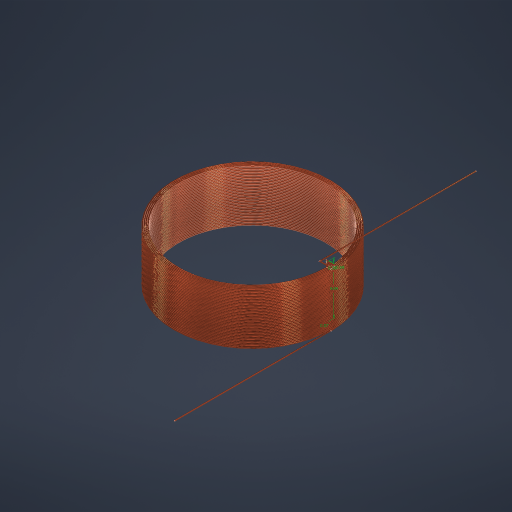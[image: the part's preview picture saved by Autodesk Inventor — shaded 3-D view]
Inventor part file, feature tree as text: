
AUTODESK INVENTOR PART (.ipt)
format: ipt  version: 2024.2 (Build 282272000, 272)  size: 3,379,712 bytes
history: native  units: mm
features: other x9, sketch x9, chamfer x8, sweep x4, extrude x1
ambient origin geometry x8: Origin, YZ Plane, XZ Plane, XY Plane, X Axis, Y Axis, Z Axis, Center Point
bodies: Volumenkörper1 (feature_tree), Volumenkörper2 (feature_tree), Volumenkörper3 (feature_tree), Volumenkörper4 (feature_tree), Volumenkörper5 (feature_tree), Volumenkörper6 (feature_tree), Volumenkörper7 (feature_tree), Volumenkörper8 (feature_tree), Volumenkörper9 (feature_tree)
feature tree (31):
  other  "Spirale1"
  other  "Spirale2"
  other  "Spirale3"
  other  "Spirale4"
  sweep  "Sweeping1"
  other  "3D-Skizze7"
  sketch  "Skizze15"  dims[d26=0.101mm d27=4.0mm d28=400.0mm d29=0.0mm d30=90.0deg d31=90.0deg d32=0.0mm d33=0.0mm]
  sweep  "Sweeping2"
  sweep  "Sweeping3"
  chamfer  "Fasen4"  Distance=0.7mm
  chamfer  "Fasen5"  [1 undecoded]
  chamfer  "Fasen6"  Distance=0.39mm
  chamfer  "Fasen7"  Distance=0.59mm
  chamfer  "Fasen8"  Distance=4.04mm
  chamfer  "Fasen9"  Distance=0.57mm
  extrude  "Extrusion1"  TaperAngle=0.0deg  [1 undecoded]
  chamfer  "Fasen10"  Distance=0.37mm
  sweep  "Sweeping4"
  chamfer  "Fasen11"  Distance=0.33mm
  other  "Kombinieren3"
  sketch  "Skizze1"  dims[d0=0.1mm d1=6.0mm]
  other  "3D-Skizze5"
  sketch  "Skizze14"  dims[d16=0.1mm d17=5.6995mm d18=0.101mm d19=4.0mm d20=400.0mm d21=0.0mm d22=90.0deg d23=90.0deg d24=0.0mm d25=0.0mm]
  sketch  "Skizze16"  dims[d34=0.101mm d35=4.0mm d36=400.0mm d37=0.0mm d38=90.0deg d39=90.0deg d40=0.0mm d41=0.0mm d45=0.5mm]
  other  "3D-Skizze8"
  sketch  "Skizze17"  dims[d46=0.8mm]
  sketch  "Skizze18"  dims[d47=4.04mm]
  other  "3D-Skizze9"
  sketch  "Skizze19"  dims[d48=0.8mm d49=0.7mm d50=0.0mm d51=0.0mm d57=0.39mm d58=0.59mm d59=4.04mm d60=0.57mm d61=0.0mm d62=0.0mm d65=0.37mm d66=4.04mm d67=0.33mm d68=0.27mm d69=0.0mm d70=0.0mm d71=0.08mm d72=0.08mm d73=0.08mm d83=0.01mm d84=2.0mm d85=45.0deg d86=0.01mm d87=2.0mm d88=45.0deg d89=0.01mm d90=2.0mm d91=45.0deg d92=0.01mm d93=2.0mm d94=45.0deg d95=0.01mm d96=2.0mm d97=45.0deg d98=0.01mm d99=2.0mm d100=45.0deg d101=0.08mm d102=12.0mm d103=0.0mm d104=0.01mm d105=2.0mm d106=45.0deg d107=0.17mm d108=0.7mm d109=12.0mm d110=0.08mm d111=0.0mm d112=0.0mm d113=0.01mm d114=2.0mm d115=45.0deg]
  sketch  "Skizze3"  dims[d2=0.101mm d3=4.0mm d4=400.0mm d5=0.0mm d6=0.0mm d7=90.0deg d8=0.0mm d9=0.0mm d12=0.1mm d13=5.8995mm]
  sketch  "Skizze4"  dims[d14=0.1mm d15=5.7995mm]
note: 2 required parameter values undecoded (feature->parameter linkage not recoverable at this tier; creation-order binding heuristic only, values carry confidence <= 0.55)
